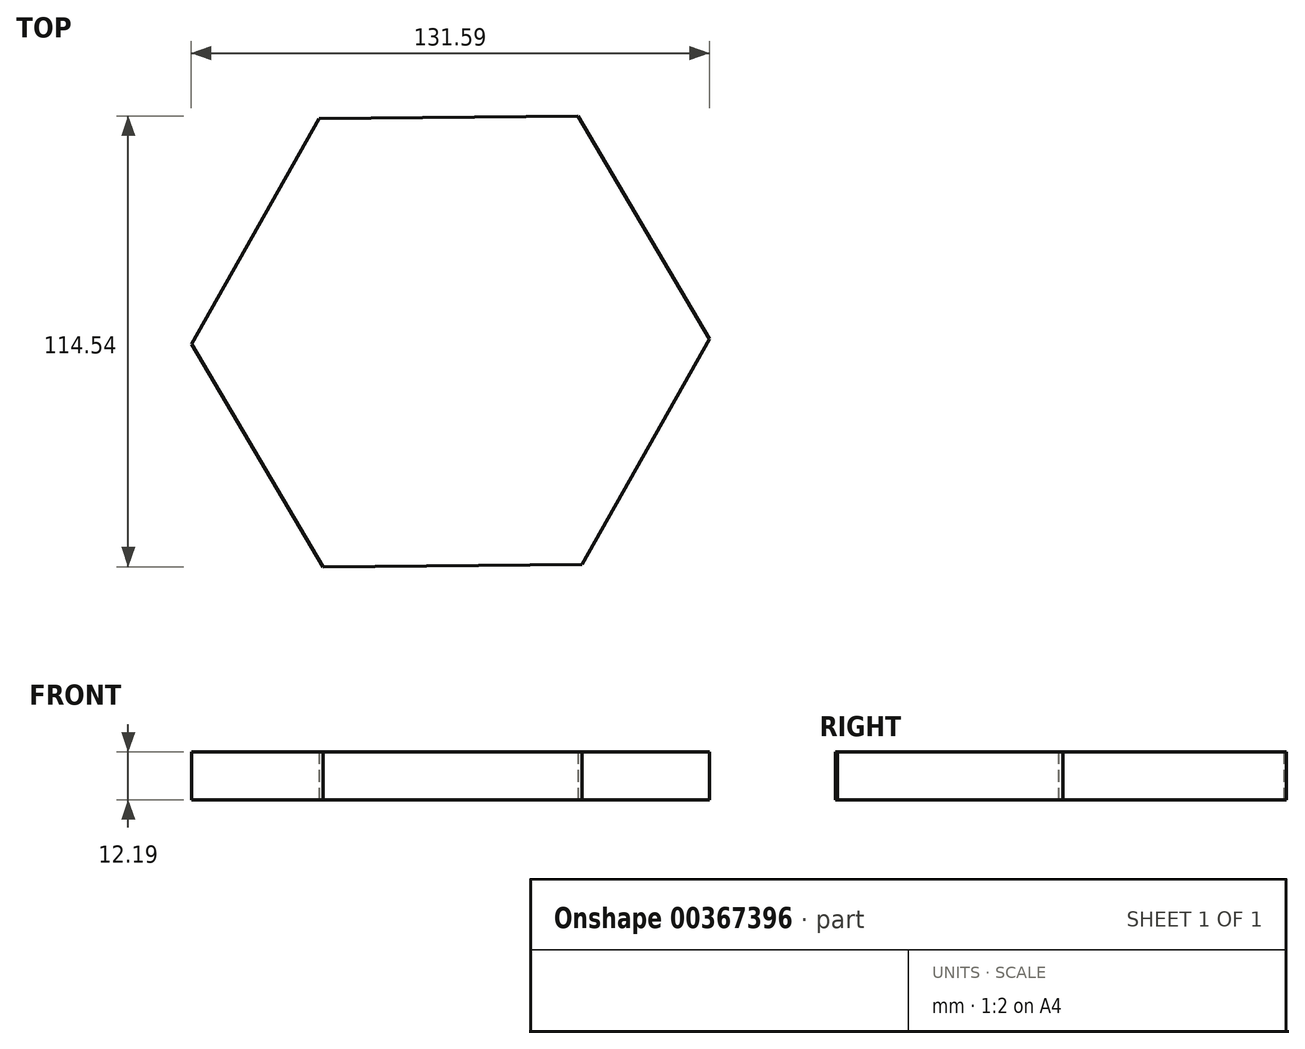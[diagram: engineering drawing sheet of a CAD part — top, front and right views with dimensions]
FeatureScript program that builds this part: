
annotation { "Feature Type Name" : "Feature", "Feature Type Description" : "" }
export const myFeature = defineFeature(function(context is Context, id is Id, definition is map)
    precondition{}
    {
        {
            var Q0;
            Q0=qCreatedBy(makeId("Top.planeOp"),FACE);
            var sketch = newSketch(context, id + "F0", { "sketchPlane" : qUnion([Q0])});
            skCircle(sketch, "E0.cCircle", {"center": v(2.66, 0) * mm, "radius": 56.98 * mm, "construction": true});
            skLineSegment(sketch, "E0.0", {"start": v(-63.14, -0.59) * mm, "end": v(-30.75, 56.68) * mm});
            skLineSegment(sketch, "E0.1", {"start": v(-30.75, 56.68) * mm, "end": v(35.04, 57.27) * mm});
            skLineSegment(sketch, "E0.2", {"start": v(35.04, 57.27) * mm, "end": v(68.45, 0.59) * mm});
            skLineSegment(sketch, "E0.3", {"start": v(68.45, 0.59) * mm, "end": v(36.06, -56.68) * mm});
            skLineSegment(sketch, "E0.4", {"start": v(36.06, -56.68) * mm, "end": v(-29.73, -57.27) * mm});
            skLineSegment(sketch, "E0.5", {"start": v(-29.73, -57.27) * mm, "end": v(-63.14, -0.59) * mm});
            skPoint(sketch, "E0.0.midPoint", {"position": v(-46.94, 28.05) * mm});
            skSolve(sketch);
        }
        {
            var Q0;
            Q0 = qSketchRegion(id + "F0", true);
            extrude(context, id + "F1", {"entities" : qUnion([Q0]), "depth" : 12.2 * mm});
        }
    });
